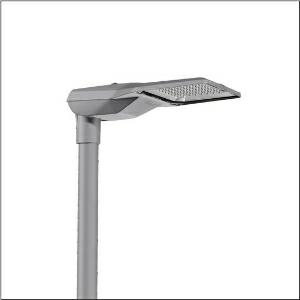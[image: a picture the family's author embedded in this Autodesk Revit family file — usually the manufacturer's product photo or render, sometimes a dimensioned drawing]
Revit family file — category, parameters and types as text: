
# Revit family: streetlight_sl_21_midi___p0_8ab_5xe3r33s08mb_a55a
name_source: partatom
category: Lighting Fixtures
units: mm (PartAtom-declared; Revit-internal decimal feet)

## family parameters
Cut with Voids When Loaded = No
Host = Face
Light Source = No
Part Type = Normal
Room Calculation Point = No
Round Connector Dimension = Use Diameter
Shared = No

## types (1)
- --- (1 x LED, 15870 lm, 136 W, 3000K)
    Apparent Load = 136 VA
    CIE Flux Codes = 36 71 98 100 100
    Color Rendering = 70
    Color Temperature = 3000K
    Default Elevation = 1800 mm
    Description = Streetlight SL 21 midi, mast luminaire, primary light control with lens, of PMMA, primary optical cover: cover, of toughened safety glass, transparent, light distribution: P0.8aB, light emission: direct distribution, primary light characteristic: asymmetric, installation type: post-top, side-entry, LED, High Power LED, rated luminous flux: 15.870lm, luminous efficacy: 117lm/W, light colour: 730, colour temperature: 3000K, control gear: D4i, control: pre-setting: logarithmic dimming characteristic, flexible luminous flux parameterisation, time-dependent luminous flux control, constant luminous flux control, overheat protection, mains connection: 230..240V, AC, 50/60Hz, start of lifetime: 136W, end of service life: 142W, reduction: 61W, luminaire housing, of diecast aluminium, powder-coated, Siteco® metallic grey (DB 702S), corrosivity category C5 mid according to DIN EN ISO 12944, multi-level sealing system, sealing non-destructively replaceable, inclination adjustable: 0°, 5°, 10°, 15°, please order mast flange separately, length: 644mm, width: 335mm, height: 110mm, mast flange for spigot size: 42mm (side-entry): 5XC10008XM4, 60/48mm (side-entry/post-top): 5XC10108XM2, 76/60mm (side-entry/post-top): 5XC10108XM1, mounting height: 4..8m, Smart Interface above, protection rating (complete): IP66, insulation class (complete): insulation class II (safety insulation), certification: CE, ENEC, ENEC+, VDE, impact resistance: IK10, permissible operating ambient temperature for outdoor applications: -40..+50°C, standard-compliant lighting for roads and squares, packaging unit: 1 piece

Light Distribution: P0.8aB
    Height = 111 mm
    Lamp = 1 x LED
    Lamp Light Flux = 15870 lm
    Lamp Power = 136 W
    Lamp count = 1
    Length = 644 mm
    Luminous efficacy = 117 lm/W
    Manufacturer = Siteco
    ModVariant = No
    Model = 5XE3R33S08MB
    Number of Poles = 1
    OnlyDefault = Yes
    Power Factor = 1
    Product Name = Streetlight SL 21 midi | P0.8aB
    Product group = mast luminaire | pylon top
    ProductGroupID = 6100
    Protection Class = Protection class II
    Protection Degree = IP 66
    RLX_Detail_Level = 1
    RLX_Emergency_Light_Flux = 0 lm
    RLX_Emergency_Type = 0
    RLX_Emergency_Type_DB = No
    RlxData = <blob elided: 26557 chars, md5=358477e7>
    Socket = socket
    Standby Power = 0 W
    System Light Flux = 15870 lm
    System Power = 136 W
    Type Comments = factory setting: luminous flux: 100 % | dim-lin: 254 | 695 mA
    Type Image = l_1004302.jpg
    URL = http://relux.com
    VarID = @adj_075006
    Voltage = 0 V
    Weight = 0.00 kg
    Width = 336 mm

## geometry (parser evidence)
native form markers: Blend x4, Sweep x11
no freeform markers — native parametric forms only
